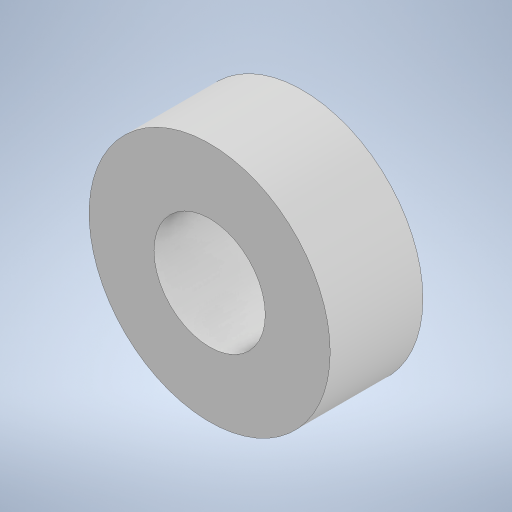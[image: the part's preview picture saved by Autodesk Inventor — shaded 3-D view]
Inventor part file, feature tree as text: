
AUTODESK INVENTOR PART (.ipt)
format: ipt  version: 2023 (Build 270158000, 158)  size: 237,568 bytes
history: native  units: in
note: dims shown in document units (in); Inventor stores cm internally (conversion verified against a paired STEP export)
features: extrude x2, sketch x2
ambient origin geometry x8: Origin, YZ Plane, XZ Plane, XY Plane, X Axis, Y Axis, Z Axis, Center Point
bodies: Solid1 (feature_tree)
feature tree (4):
  extrude  "Extrusion1"  Depth=4.7244in
  extrude  "Extrusion2"  Depth=0.1969in
  sketch  "Sketch1"  dims[d0=0.5118in d5=4.7244in]
  sketch  "Sketch2"  dims[d6=0.1969in d7=0.0in d8=4.7244in d9=0.2362in d10=8.2677in d12=360.0deg d14=0.0in d15=0.0in]
